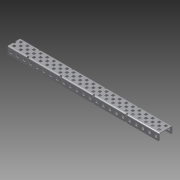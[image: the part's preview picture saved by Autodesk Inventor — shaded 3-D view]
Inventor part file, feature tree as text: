
AUTODESK INVENTOR PART (.ipt)
format: ipt  version: 2012 (Build 160160000, 160)  size: 1,447,424 bytes
history: native  units: in
note: dims shown in document units (in); Inventor stores cm internally (conversion verified against a paired STEP export)
features: other x1, imported_body x1, plane x1, split x1
ambient origin geometry x8: Origin, YZ Plane, XZ Plane, XY Plane, X Axis, Y Axis, Z Axis, Center Point
feature tree (4):
  parser-record x1  (decoder bookkeeping rows leaked as tree rows — omitted from the tree; the rows remain in map.json)
  imported_body  "Base1"
  plane  "Work Plane1"
  split  "Split2"
